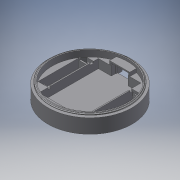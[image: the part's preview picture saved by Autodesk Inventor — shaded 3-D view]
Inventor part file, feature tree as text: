
AUTODESK INVENTOR PART (.ipt)
format: ipt  version: 2016 SP2 (Build 200236200, 236)  size: 521,216 bytes
history: native  units: mm
features: sketch x12, extrude x8, revolve x3, thread x2, other x1
ambient origin geometry x8: Origin, YZ Plane, XZ Plane, XY Plane, X Axis, Y Axis, Z Axis, Center Point
bodies: Volumenkörper1 (feature_tree), Volumenkörper3 (feature_tree)
feature tree (26):
  revolve  "Umdrehung1"
  thread  "Gewinde1"  [1 undecoded]
  extrude  "Extrusion1"  Depth=20.0mm
  extrude  "Extrusion2"  Depth=2.3mm
  extrude  "Extrusion3"  TaperAngle=90.0deg  [1 undecoded]
  thread  "Gewinde2"  [1 undecoded]
  revolve  "Umdrehung4"
  revolve  "Umdrehung5"
  other  "Spirale2"
  extrude  "Extrusion4"  Depth=35.35mm
  extrude  "Extrusion5"  Depth=8.4mm
  extrude  "Extrusion6"  Depth=10.5mm TaperAngle=0.0deg
  extrude  "Extrusion7"  Depth=3.0mm
  extrude  "Extrusion8"  Depth=3.0mm
  sketch  "Skizze1"  dims[d1=20.0mm d2=5.0mm]
  sketch  "Skizze5"  dims[d3=2.0mm d4=2.3mm]
  sketch  "Skizze6"  dims[d5=3.0mm d6=90.0deg d7=10.0mm d8=0.0mm]
  sketch  "Skizze7"  dims[d16=60.0deg]
  sketch  "Skizze8"  dims[d28=50.7mm d29=70.7mm d32=11.0mm d33=11.0mm d34=48.3mm d35=48.3mm d36=1.2mm d37=1.2mm d38=0.8mm d39=0.8mm d40=0.8mm d41=3.0mm d42=3.75mm d43=2.0mm d44=3.0mm d45=0.5mm d46=0.5mm d47=0.8mm d48=0.5mm d49=3.0mm d50=3.75mm d51=2.0mm d52=0.5mm d53=3.0mm d54=0.8mm d55=0.8mm d56=1.6mm d57=1.0mm d58=1.0mm d59=1.0mm d60=1.0mm d61=1.0mm d62=1.0mm d63=1.6mm d64=0.5mm d65=35.35mm]
  sketch  "Skizze9"  dims[d66=25.35mm d67=8.4mm]
  sketch  "Skizze10"  dims[d68=11.0mm d69=10.5mm d70=0.0mm]
  sketch  "Skizze11"  dims[d71=3.0mm d72=3.0mm]
  sketch  "Skizze12"  dims[d73=3.8mm d74=0.0mm d75=3.0mm]
  sketch  "Skizze13"  dims[d76=3.0mm]
  sketch  "Skizze14"  dims[d77=3.8mm d78=0.0mm]
  sketch  "Skizze15"  dims[d79=10.0mm d80=0.0mm d81=60.0deg d82=0.320166mm d83=0.320166mm d86=2.0mm d88=60.0deg d90=0.0mm d91=0.0mm d92=2.002mm d93=7.0mm d94=10.0mm d95=0.0mm d96=0.0mm d97=0.0mm d98=0.0mm d99=0.0mm d100=19.0mm d101=11.5mm d102=7.0mm d103=0.0mm d104=21.0mm d105=15.5mm d106=9.5mm d107=0.0mm d108=4.0mm d109=4.0mm d110=5.75mm d111=5.75mm d112=3.0mm d113=3.0mm d114=4.0mm d115=4.0mm d116=2.0mm d117=0.0mm d118=20.0mm d119=5.0mm d120=0.0mm d121=1.5mm d122=9.75mm d123=0.0mm]
note: 3 required parameter values undecoded (feature->parameter linkage not recoverable at this tier; creation-order binding heuristic only, values carry confidence <= 0.55)
